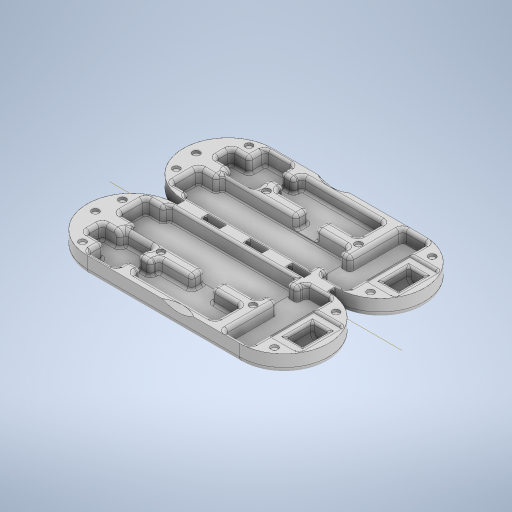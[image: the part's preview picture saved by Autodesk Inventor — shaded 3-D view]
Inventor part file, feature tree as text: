
AUTODESK INVENTOR PART (.ipt)
format: ipt  version: 2023 (Build 270158030, 158C)  size: 1,200,128 bytes
history: native  units: mm
features: fillet x14, extrude x10, sketch x10, mirror x1
ambient origin geometry x8: Origin, YZ Plane, XZ Plane, XY Plane, X Axis, Y Axis, Z Axis, Center Point
bodies: Solid1 (feature_tree)
feature tree (35):
  extrude  "Extrusion1"  Depth=76.0mm
  extrude  "Extrusion2"  Depth=33.0mm
  extrude  "Extrusion3"  Depth=108.0mm
  extrude  "Extrusion4"  Depth=5.0mm
  extrude  "Extrusion5"  Depth=20.0mm
  fillet  "Fillet1"  Radius=108.0mm
  extrude  "Extrusion6"  Depth=33.0mm
  fillet  "Fillet2"  Radius=4.0mm
  fillet  "Fillet3"  Radius=24.0mm
  fillet  "Fillet4"  Radius=5.0mm
  fillet  "Fillet5"  Radius=14.0mm
  fillet  "Fillet6"  Radius=24.0mm
  fillet  "Fillet7"  Radius=3.0mm
  fillet  "Fillet8"  Radius=12.5mm
  fillet  "Fillet9"  Radius=70.0mm
  fillet  "Fillet10"  Radius=22.0mm
  fillet  "Fillet11"  Radius=7.0mm
  fillet  "Fillet12"  Radius=11.0mm
  extrude  "Extrusion7"  Depth=3.0mm
  extrude  "Extrusion8"  Depth=9.0mm
  fillet  "Fillet13"  Radius=22.0mm
  extrude  "Extrusion9"  Depth=22.5mm
  mirror  "Mirror1"
  fillet  "Fillet14"  Radius=14.0mm
  extrude  "Extrusion10"  Depth=25.0mm
  sketch  "Sketch1"  dims[d0=3.0mm d1=3.0mm d3=76.0mm d4=76.0mm]
  sketch  "Sketch2"  dims[d5=15.0mm d6=0.0mm d7=33.0mm]
  sketch  "Sketch3"  dims[d8=3.0mm d9=108.0mm]
  sketch  "Sketch4"  dims[d10=5.0mm d11=5.0mm]
  sketch  "Sketch5"  dims[d12=15.0mm d13=20.0mm d14=108.0mm]
  sketch  "Sketch6"  dims[d15=15.0mm d17=33.0mm d18=4.0mm d19=24.0mm d20=5.0mm d21=14.0mm d22=24.0mm d23=3.0mm d24=12.5mm d25=0.0mm d26=70.0mm d27=22.0mm d28=7.0mm d29=11.0mm]
  sketch  "Sketch7"  dims[d30=70.0mm d31=3.0mm]
  sketch  "Sketch8"  dims[d32=3.0mm d33=9.0mm d34=22.0mm]
  sketch  "Sketch9"  dims[d35=11.0mm d36=0.0mm d37=22.5mm d38=14.0mm]
  sketch  "Sketch10"  dims[d39=7.0mm d40=26.75mm d41=26.75mm d42=14.0mm d43=0.0mm d44=7.0mm d45=7.0mm d46=4.0mm d47=6.0mm d48=2.0mm d49=0.0mm d50=1.98mm d51=17.0mm d52=17.0mm d53=8.0mm d54=25.0mm d55=7.0mm d56=8.0mm d57=12.0mm d58=0.0mm d59=3.0mm d60=3.0mm d61=2.0mm d62=2.0mm d63=5.0mm d64=5.0mm d65=2.0mm d66=1.0mm d67=2.0mm d68=2.0mm d69=2.0mm d70=1.0mm d73=20.0mm d74=20.0mm d75=20.0mm d76=1.0mm d77=20.0mm d78=16.0mm d79=16.0mm d80=16.0mm d81=1.0mm d82=0.0mm d86=0.0mm d87=0.0mm d88=1.0mm d89=5.0mm d90=6.0mm d91=6.0mm d92=6.0mm d93=6.0mm d94=9.0mm d95=20.0mm d96=6.0mm d97=6.0mm d98=9.0mm d99=6.0mm d100=6.0mm d101=2.05mm d102=0.0mm d103=130.0mm d104=65.0mm d105=65.0mm d106=4.08392mm d107=5.0mm d108=50.0mm d109=12.5mm d110=100.0mm d111=20.0mm d113=360.0deg d115=0.009mm d116=-8.726646mm d117=6.0mm d118=6.0mm d119=6.0mm d120=40.0mm d121=9.0mm d122=6.0mm d123=8.0mm d124=6.5mm]
